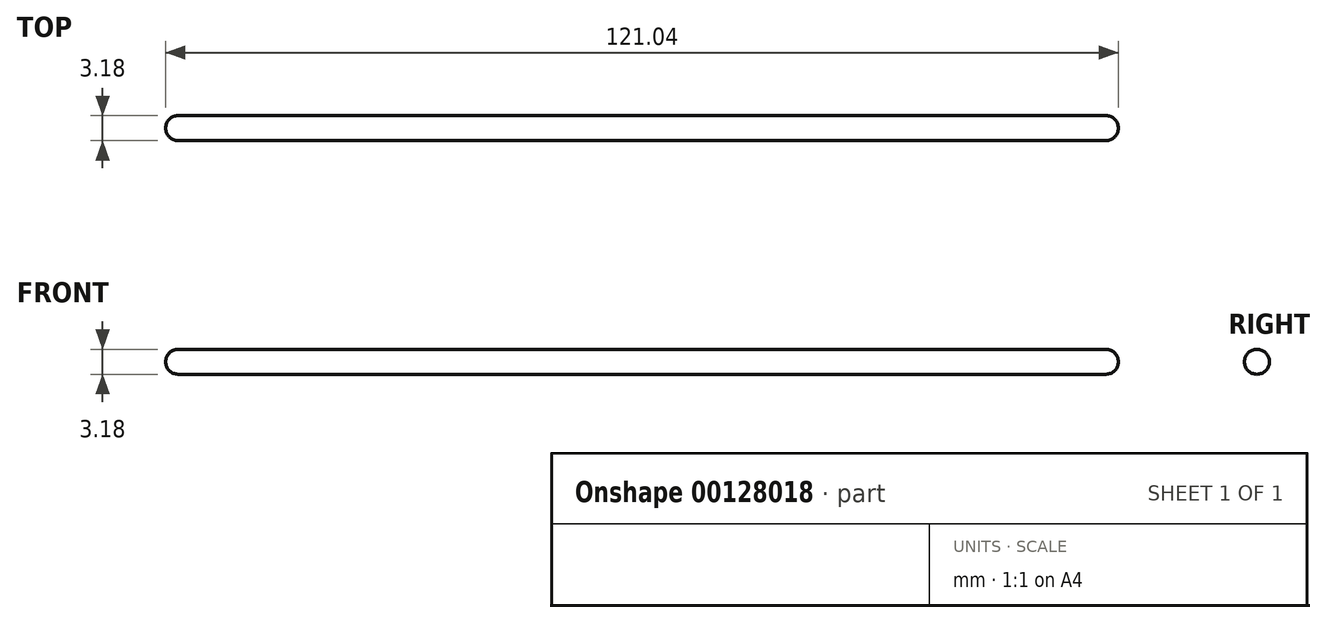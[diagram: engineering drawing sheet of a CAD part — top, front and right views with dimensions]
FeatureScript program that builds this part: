
annotation { "Feature Type Name" : "Feature", "Feature Type Description" : "" }
export const myFeature = defineFeature(function(context is Context, id is Id, definition is map)
    precondition{}
    {
        {
            var Q0;
            Q0=qCreatedBy(makeId("Front.planeOp"),FACE);
            var sketch = newSketch(context, id + "F0", { "sketchPlane" : qUnion([Q0])});
            skLineSegment(sketch, "E0", {"start": v(-58.93, 0) * mm, "end": v(58.93, 0) * mm});
            skArc(sketch, "E1", {"start": v(-58.93, 1.59) * mm, "mid": v(-60.05, 1.12) * mm, "end": v(-60.52, 0) * mm});
            skArc(sketch, "E2", {"start": v(60.52, 0) * mm, "mid": v(60.05, 1.12) * mm, "end": v(58.93, 1.59) * mm});
            skLineSegment(sketch, "E3", {"start": v(-58.93, 0) * mm, "end": v(-60.52, 0) * mm});
            skLineSegment(sketch, "E4", {"start": v(58.93, 0) * mm, "end": v(60.52, 0) * mm});
            skLineSegment(sketch, "E5", {"start": v(-58.93, 1.59) * mm, "end": v(58.93, 1.59) * mm});
            skSolve(sketch);
        }
        {
            var Q0;
            Q0=makeQuery(id+"F0.imprint","IMPRINT",FACE,{"disambiguationData":[TD([[makeQuery(id+"F0.imprint","IMPRINT",EDGE,{"derivedFrom":sQuery(id+"F0.wireOp",EDGE,"E0")}),1.0]])]});
            var Q1;
            Q1=sQuery(id+"F0.wireOp",EDGE,"E0");
            revolve(context, id + "F1", {"entities" : qUnion([Q0]), "axis" : qUnion([Q1]), "revolveType" : RevolveType.FULL});
        }
    });
